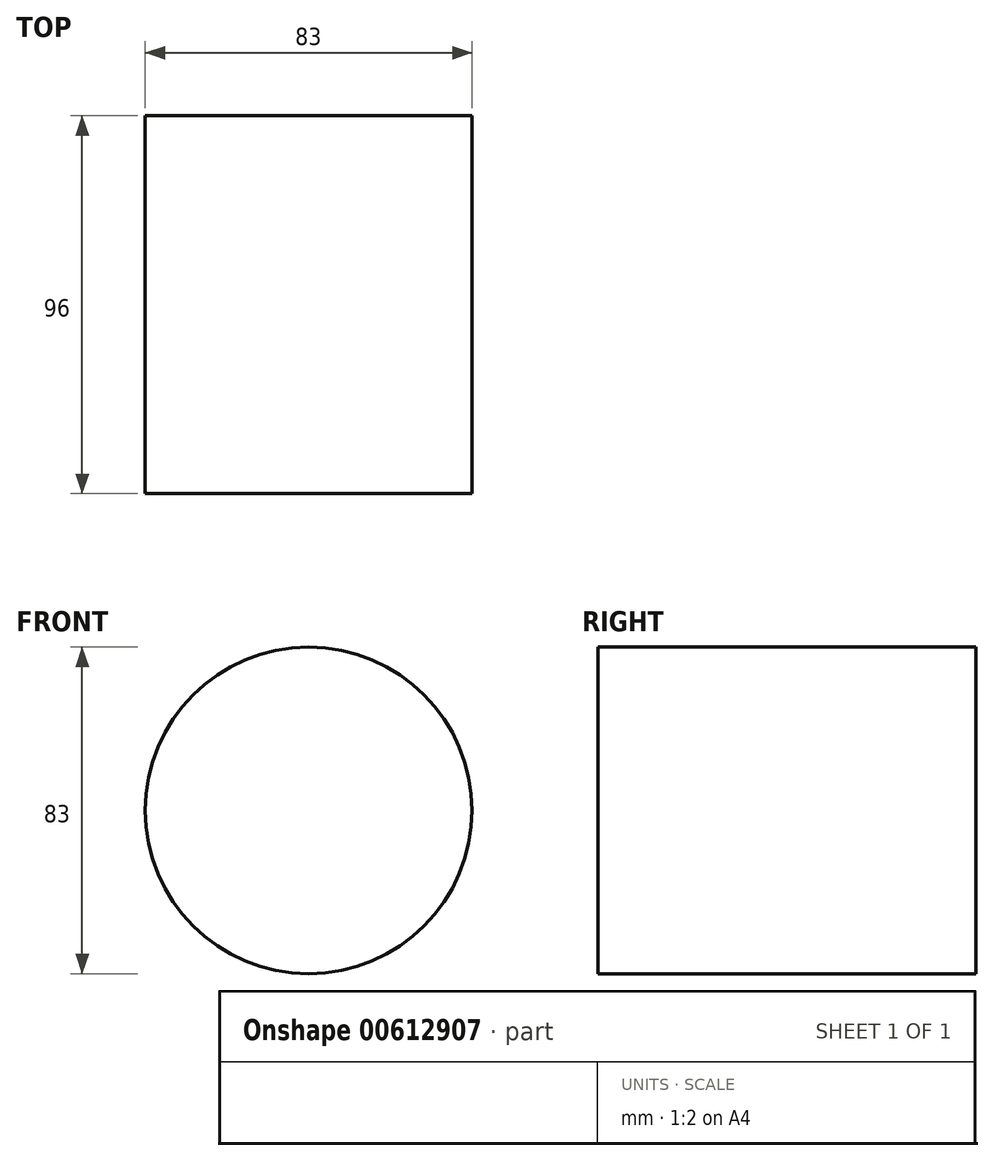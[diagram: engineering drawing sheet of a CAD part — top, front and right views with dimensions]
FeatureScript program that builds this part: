
annotation { "Feature Type Name" : "Feature", "Feature Type Description" : "" }
export const myFeature = defineFeature(function(context is Context, id is Id, definition is map)
    precondition{}
    {
        {
            var Q0;
            Q0=qCreatedBy(makeId("Front.planeOp"),FACE);
            var sketch = newSketch(context, id + "F0", { "sketchPlane" : qUnion([Q0])});
            skCircle(sketch, "E0", {"center": v(0, -1.62) * mm, "radius": 41.5 * mm});
            skSolve(sketch);
        }
        {
            var Q0;
            Q0 = qSketchRegion(id + "F0", true);
            extrude(context, id + "F1", {"entities" : qUnion([Q0]), "depth" : 96 * mm, "offsetDistance" : 25 * mm});
        }
    });
